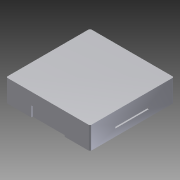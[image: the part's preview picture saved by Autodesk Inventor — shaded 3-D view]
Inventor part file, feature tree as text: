
AUTODESK INVENTOR PART (.ipt)
format: ipt  version: 2014 (Build 180170000, 170)  size: 139,264 bytes
history: native  units: in
note: dims shown in document units (in); Inventor stores cm internally (conversion verified against a paired STEP export)
features: other x35, extrude x6, sketch x6
ambient origin geometry x8: Origin, YZ Plane, XZ Plane, XY Plane, X Axis, Y Axis, Z Axis, Center Point
bodies: Solid1 (feature_tree)
feature tree (47):
  extrude  "Extrusion1"  Depth=0.2364in TaperAngle=0.0deg
  extrude  "Extrusion2"  Depth=0.2364in TaperAngle=0.0deg
  extrude  "Extrusion3"  Depth=0.2364in TaperAngle=0.0deg
  extrude  "Extrusion4"  [1 undecoded]
  extrude  "Extrusion5"  [1 undecoded]
  extrude  "Extrusion6"  [1 undecoded]
  other  "lens_to_bicol_led_1_XY"
  other  "lens_to_bicol_led_1_YZ"
  other  "lens_to_bicol_led_1_ZX"
  other  "lens_to_bicol_led_1_X"
  other  "lens_to_bicol_led_1_Y"
  other  "lens_to_bicol_led_1_Z"
  other  "lens_to_bicol_led_1_Center"
  other  "lens_to_bicol_led_2_XY"
  other  "lens_to_bicol_led_2_YZ"
  other  "lens_to_bicol_led_2_ZX"
  other  "lens_to_bicol_led_2_X"
  other  "lens_to_bicol_led_2_Y"
  other  "lens_to_bicol_led_2_Z"
  other  "lens_to_bicol_led_2_Center"
  other  "lens_to_insert_XY"
  other  "lens_to_insert_YZ"
  other  "lens_to_insert_ZX"
  other  "lens_to_insert_X"
  other  "lens_to_insert_Y"
  other  "lens_to_insert_Z"
  other  "lens_to_insert_Center"
  other  "lens_to_led_XY"
  other  "lens_to_led_YZ"
  other  "lens_to_led_ZX"
  other  "lens_to_led_X"
  other  "lens_to_led_Y"
  other  "lens_to_led_Z"
  other  "lens_to_led_Center"
  other  "lens_to_body_XY"
  other  "lens_to_body_YZ"
  other  "lens_to_body_ZX"
  other  "lens_to_body_X"
  other  "lens_to_body_Y"
  other  "lens_to_body_Z"
  other  "lens_to_body_Center"
  sketch  "Sketch_31"
  sketch  "Sketch_4"  dims[d0=0.591in d1=0.0in d2=0.2364in d3=0.0in]
  sketch  "Sketch_5"  dims[d4=0.2364in d5=0.0in d6=0.2364in d7=0.0in]
  sketch  "Sketch_14"
  sketch  "Sketch_15"
  sketch  "Sketch_8"  dims[d8=0.2364in d9=0.0in d10=0.414in d11=0.0in]
note: 3 required parameter values undecoded (feature->parameter linkage not recoverable at this tier; creation-order binding heuristic only, values carry confidence <= 0.55)
